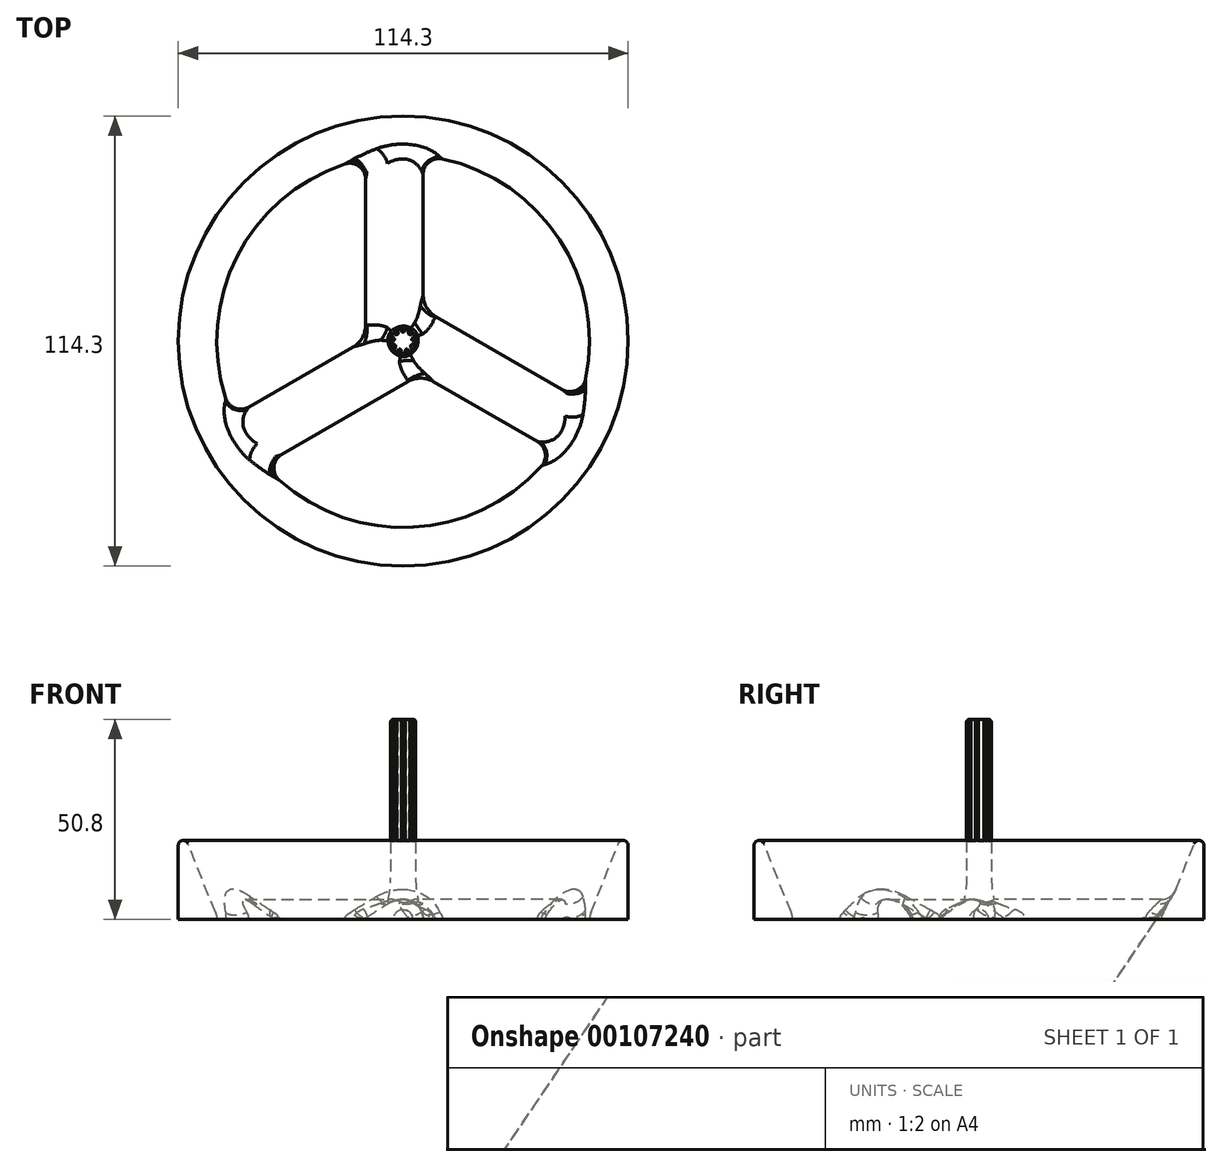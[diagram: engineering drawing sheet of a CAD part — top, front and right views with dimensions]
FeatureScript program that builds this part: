
annotation { "Feature Type Name" : "Feature", "Feature Type Description" : "" }
export const myFeature = defineFeature(function(context is Context, id is Id, definition is map)
    precondition{}
    {
        {
            var Q0;
            Q0=qCreatedBy(makeId("Front.planeOp"),FACE);
            var sketch = newSketch(context, id + "F0", { "sketchPlane" : qUnion([Q0])});
            skLineSegment(sketch, "E0", {"start": v(0, 0) * mm, "end": v(0, 50.8) * mm});
            skPoint(sketch, "E1.visualSharp", {"position": v(57.15, 25.4) * mm});
            skPoint(sketch, "E2.visualSharp", {"position": v(3.17, 50.8) * mm});
            skPoint(sketch, "E3.visualSharp", {"position": v(57.15, 0) * mm});
            skLineSegment(sketch, "E4.trimOffspring", {"start": v(3.17, -2.8) * mm, "end": v(3.17, -2.92) * mm});
            skArc(sketch, "E5", {"start": v(5.08, 0) * mm, "mid": v(3.6, 3.6) * mm, "end": v(0, 5.08) * mm});
            skLineSegment(sketch, "E6", {"start": v(57.15, 18.8) * mm, "end": v(57.15, 0) * mm});
            skLineSegment(sketch, "E7", {"start": v(57.15, 0) * mm, "end": v(47.35, 0) * mm});
            skLineSegment(sketch, "E8", {"start": v(47.7, 1.75) * mm, "end": v(54.7, 19.28) * mm});
            skArc(sketch, "E9", {"start": v(47.7, 1.75) * mm, "mid": v(47.44, 0.9) * mm, "end": v(47.35, 0) * mm});
            skPoint(sketch, "E10.orphan", {"position": v(47, 0) * mm});
            skArc(sketch, "E11.filletArc", {"start": v(57.15, 18.8) * mm, "mid": v(56.12, 20.05) * mm, "end": v(54.7, 19.28) * mm});
            skEllipticalArc(sketch, "E12", {});
            skLineSegment(sketch, "E13", {"start": v(-6.35, 0) * mm, "end": v(-2.48, 0) * mm});
            skPoint(sketch, "E14.orphan", {"position": v(6.35, 0) * mm});
            skLineSegment(sketch, "E15", {"start": v(3.18, 50.16) * mm, "end": v(3.18, 3.97) * mm});
            skLineSegment(sketch, "E16", {"start": v(2.54, 50.8) * mm, "end": v(0, 50.8) * mm});
            skArc(sketch, "E17.filletArc", {"start": v(3.17, 50.16) * mm, "mid": v(2.99, 50.61) * mm, "end": v(2.54, 50.8) * mm});
            skArc(sketch, "E18", {"start": v(2.48, 0) * mm, "mid": v(0, 2.48) * mm, "end": v(-2.48, 0) * mm});
            skLineSegment(sketch, "E19.trimOffspring", {"start": v(2.48, 0) * mm, "end": v(5.08, 0) * mm});
            skLineSegment(sketch, "E20", {"start": v(-2.48, 0) * mm, "end": v(2.48, 0) * mm});
            skArc(sketch, "E21", {"start": v(-9.24, 0.53) * mm, "mid": v(-9.45, 0.3) * mm, "end": v(-9.53, 0) * mm});
            skLineSegment(sketch, "E22", {"start": v(-9.24, 0.53) * mm, "end": v(-4.01, 3.94) * mm});
            skLineSegment(sketch, "E23", {"start": v(-6.35, 0) * mm, "end": v(-9.53, 0) * mm});
            skArc(sketch, "E24", {"start": v(3.17, 10.6) * mm, "mid": v(3.58, 6.12) * mm, "end": v(4.76, 1.77) * mm});
            const initialGuessF0  = {"E12": [0, 0, 0, 1, 0.00508, 0.00635, 6.283185307179586, 0.6836937466880189]};
            skSetInitialGuess(sketch, initialGuessF0);
            skSolve(sketch);
        }
        {
            var Q0;
            Q0=makeQuery(id+"F0.imprint","IMPRINT",FACE,{"disambiguationData":[TD([[makeQuery(id+"F0.imprint","IMPRINT",EDGE,{"derivedFrom":sQuery(id+"F0.wireOp",EDGE,"E6")}),-1.0]])]});
            var Q1;
            {var subQ0=sQuery(id+"F0.wireOp",EDGE,"E16");Q1=makeQuery(id+"F0.imprint","IMPRINT",FACE,{"disambiguationData":[TD([[makeQuery(id+"F0.imprint","IMPRINT",EDGE,{"derivedFrom":subQ0}),1.0]])]});}
            var Q2;
            {var subQ0=sQuery(id+"F0.wireOp",EDGE,"E13");var subQ3=sQuery(id+"F0.wireOp",EDGE,"E5");var subQ5=makeQuery(id+"F0.imprint","INTERSECT",VERTEX,{"derivedFrom":[subQ3,subQ0]});Q2=makeQuery(id+"F0.imprint","IMPRINT",FACE,{"disambiguationData":[TD([[makeQuery(id+"F0.imprint","IMPRINT",EDGE,{"disambiguationData":[TD([[subQ5,-1.0]])],"derivedFrom":subQ3}),1.0]])]});}
            var Q3;
            {var subQ3=sQuery(id+"F0.wireOp",EDGE,"E24");Q3=makeQuery(id+"F0.imprint","IMPRINT",FACE,{"disambiguationData":[TD([[makeQuery(id+"F0.imprint","IMPRINT",EDGE,{"derivedFrom":subQ3}),-1.0]])]});}
            var Q4;
            Q4=sQuery(id+"F0.wireOp",EDGE,"E0");
            revolve(context, id + "F1", {"entities" : qUnion([Q0, Q1, Q2, Q3]), "axis" : qUnion([Q4]), "revolveType" : RevolveType.FULL});
        }
        {
            var Q0;
            Q0=qCreatedBy(makeId("Top.planeOp"),FACE);
            var sketch = newSketch(context, id + "F2", { "sketchPlane" : qUnion([Q0])});
            skCircle(sketch, "E25.cCircle", {"center": v(0, 3.18) * mm, "radius": 0.64 * mm, "construction": true});
            skLineSegment(sketch, "E25.0", {"start": v(-1.1, 3.81) * mm, "end": v(1.1, 3.81) * mm});
            skLineSegment(sketch, "E25.1", {"start": v(0.69, 3.1) * mm, "end": v(0.27, 2.38) * mm});
            skLineSegment(sketch, "E25.2", {"start": v(-0.27, 2.38) * mm, "end": v(-0.69, 3.1) * mm});
            skPoint(sketch, "E25.0.midPoint", {"position": v(0, 3.81) * mm});
            skPoint(sketch, "E26.visualSharp", {"position": v(0, 1.9) * mm});
            skArc(sketch, "E26.filletArc", {"start": v(-0.27, 2.38) * mm, "mid": v(0, 2.22) * mm, "end": v(0.27, 2.38) * mm});
            skLineSegment(sketch, "E27.1.1", {"start": v(-1.46, 2.82) * mm, "end": v(-1.32, 2) * mm});
            skArc(sketch, "E27.1.2", {"start": v(-1.74, 1.65) * mm, "mid": v(-1.43, 1.7) * mm, "end": v(-1.32, 2) * mm});
            skLineSegment(sketch, "E27.1.3", {"start": v(-1.74, 1.65) * mm, "end": v(-2.52, 1.93) * mm});
            skLineSegment(sketch, "E27.2.1", {"start": v(-2.93, 1.22) * mm, "end": v(-2.3, 0.68) * mm});
            skArc(sketch, "E27.2.2", {"start": v(-2.4, 0.14) * mm, "mid": v(-2.19, 0.39) * mm, "end": v(-2.3, 0.68) * mm});
            skLineSegment(sketch, "E27.2.3", {"start": v(-2.4, 0.14) * mm, "end": v(-3.17, -0.14) * mm});
            skLineSegment(sketch, "E27.3.1", {"start": v(-3.03, -0.95) * mm, "end": v(-2.2, -0.95) * mm});
            skArc(sketch, "E27.3.2", {"start": v(-1.92, -1.43) * mm, "mid": v(-1.92, -1.11) * mm, "end": v(-2.2, -0.95) * mm});
            skLineSegment(sketch, "E27.3.3", {"start": v(-1.92, -1.43) * mm, "end": v(-2.34, -2.15) * mm});
            skLineSegment(sketch, "E27.4.1", {"start": v(-1.7, -2.68) * mm, "end": v(-1.07, -2.14) * mm});
            skArc(sketch, "E27.4.2", {"start": v(-0.56, -2.33) * mm, "mid": v(-0.76, -2.09) * mm, "end": v(-1.07, -2.14) * mm});
            skLineSegment(sketch, "E27.4.3", {"start": v(-0.56, -2.33) * mm, "end": v(-0.41, -3.15) * mm});
            skLineSegment(sketch, "E27.5.1", {"start": v(0.41, -3.15) * mm, "end": v(0.56, -2.33) * mm});
            skArc(sketch, "E27.5.2", {"start": v(1.07, -2.14) * mm, "mid": v(0.76, -2.09) * mm, "end": v(0.56, -2.33) * mm});
            skLineSegment(sketch, "E27.5.3", {"start": v(1.07, -2.14) * mm, "end": v(1.7, -2.68) * mm});
            skLineSegment(sketch, "E27.6.1", {"start": v(2.34, -2.15) * mm, "end": v(1.92, -1.43) * mm});
            skArc(sketch, "E27.6.2", {"start": v(2.2, -0.95) * mm, "mid": v(1.92, -1.11) * mm, "end": v(1.92, -1.43) * mm});
            skLineSegment(sketch, "E27.6.3", {"start": v(2.2, -0.95) * mm, "end": v(3.03, -0.95) * mm});
            skLineSegment(sketch, "E27.7.1", {"start": v(3.17, -0.14) * mm, "end": v(2.4, 0.14) * mm});
            skArc(sketch, "E27.7.2", {"start": v(2.3, 0.68) * mm, "mid": v(2.19, 0.39) * mm, "end": v(2.4, 0.14) * mm});
            skLineSegment(sketch, "E27.7.3", {"start": v(2.3, 0.68) * mm, "end": v(2.93, 1.22) * mm});
            skLineSegment(sketch, "E27.8.1", {"start": v(2.52, 1.93) * mm, "end": v(1.74, 1.65) * mm});
            skArc(sketch, "E27.8.2", {"start": v(1.32, 2) * mm, "mid": v(1.43, 1.7) * mm, "end": v(1.74, 1.65) * mm});
            skLineSegment(sketch, "E27.8.3", {"start": v(1.32, 2) * mm, "end": v(1.46, 2.82) * mm});
            skPoint(sketch, "E27.center", {"position": v(0, 0) * mm});
            skArc(sketch, "E28.trimOffspring", {"start": v(2.93, 1.22) * mm, "mid": v(2.75, 1.59) * mm, "end": v(2.52, 1.93) * mm});
            skArc(sketch, "E29", {"start": v(-2.93, 1.22) * mm, "mid": v(-3.13, 0.55) * mm, "end": v(-3.17, -0.14) * mm});
            skArc(sketch, "E30.trimOffspring", {"start": v(-3.03, -0.95) * mm, "mid": v(-2.75, -1.59) * mm, "end": v(-2.34, -2.15) * mm});
            skArc(sketch, "E31.trimOffspring", {"start": v(-1.7, -2.68) * mm, "mid": v(-1.09, -2.98) * mm, "end": v(-0.41, -3.15) * mm});
            skArc(sketch, "E32.trimOffspring", {"start": v(0.41, -3.15) * mm, "mid": v(1.09, -2.98) * mm, "end": v(1.7, -2.68) * mm});
            skArc(sketch, "E33.trimOffspring", {"start": v(2.34, -2.15) * mm, "mid": v(2.75, -1.59) * mm, "end": v(3.03, -0.95) * mm});
            skArc(sketch, "E34.trimOffspring", {"start": v(3.17, -0.14) * mm, "mid": v(3.13, 0.55) * mm, "end": v(2.93, 1.22) * mm});
            skArc(sketch, "E35.trimOffspring", {"start": v(2.52, 1.93) * mm, "mid": v(2.04, 2.43) * mm, "end": v(1.46, 2.82) * mm});
            skArc(sketch, "E36.trimOffspring", {"start": v(0.69, 3.1) * mm, "mid": v(0, 3.18) * mm, "end": v(-0.69, 3.1) * mm});
            skArc(sketch, "E37.trimOffspring", {"start": v(-1.46, 2.82) * mm, "mid": v(-2.04, 2.43) * mm, "end": v(-2.52, 1.93) * mm});
            skSolve(sketch);
        }
        {
            var Q0;
            Q0=makeQuery(id+"F2.imprint","IMPRINT",FACE,{"disambiguationData":[TD([[makeQuery(id+"F2.imprint","IMPRINT",EDGE,{"derivedFrom":sQuery(id+"F2.wireOp",EDGE,"E27.1.1")}),-1.0]])]});
            var Q1;
            Q1=makeQuery(id+"F2.imprint","IMPRINT",FACE,{"disambiguationData":[TD([[makeQuery(id+"F2.imprint","IMPRINT",EDGE,{"derivedFrom":sQuery(id+"F2.wireOp",EDGE,"E27.2.1")}),-1.0]])]});
            var Q2;
            Q2=makeQuery(id+"F2.imprint","IMPRINT",FACE,{"disambiguationData":[TD([[makeQuery(id+"F2.imprint","IMPRINT",EDGE,{"derivedFrom":sQuery(id+"F2.wireOp",EDGE,"E27.3.1")}),-1.0]])]});
            var Q3;
            Q3=makeQuery(id+"F2.imprint","IMPRINT",FACE,{"disambiguationData":[TD([[makeQuery(id+"F2.imprint","IMPRINT",EDGE,{"derivedFrom":sQuery(id+"F2.wireOp",EDGE,"E27.4.1")}),-1.0]])]});
            var Q4;
            Q4=makeQuery(id+"F2.imprint","IMPRINT",FACE,{"disambiguationData":[TD([[makeQuery(id+"F2.imprint","IMPRINT",EDGE,{"derivedFrom":sQuery(id+"F2.wireOp",EDGE,"E27.5.1")}),-1.0]])]});
            var Q5;
            Q5=makeQuery(id+"F2.imprint","IMPRINT",FACE,{"disambiguationData":[TD([[makeQuery(id+"F2.imprint","IMPRINT",EDGE,{"derivedFrom":sQuery(id+"F2.wireOp",EDGE,"E27.6.1")}),-1.0]])]});
            var Q6;
            Q6=makeQuery(id+"F2.imprint","IMPRINT",FACE,{"disambiguationData":[TD([[makeQuery(id+"F2.imprint","IMPRINT",EDGE,{"derivedFrom":sQuery(id+"F2.wireOp",EDGE,"E27.7.1")}),-1.0]])]});
            var Q7;
            Q7=makeQuery(id+"F2.imprint","IMPRINT",FACE,{"disambiguationData":[TD([[makeQuery(id+"F2.imprint","IMPRINT",EDGE,{"derivedFrom":sQuery(id+"F2.wireOp",EDGE,"E27.8.1")}),-1.0]])]});
            var Q8;
            Q8=makeQuery(id+"F2.imprint","IMPRINT",FACE,{"disambiguationData":[TD([[makeQuery(id+"F2.imprint","IMPRINT",EDGE,{"derivedFrom":sQuery(id+"F2.wireOp",EDGE,"E25.1")}),-1.0]])]});
            extrude(context, id + "F3", {"entities" : qUnion([Q0, Q1, Q2, Q3, Q4, Q5, Q6, Q7, Q8]), "depth" : 52.98 * mm, "hasSecondDirection" : true, "secondDirectionOppositeDirection" : false, "secondDirectionDepth" : 19.8 * mm});
        }
        {
            var Q0;
            Q0=makeQuery(id+"F3.opExtrude","SWEPT_BODY",BODY,{"disambiguationData":[OSD([sQuery(id+"F2.wireOp",EDGE,"E25.1"),sQuery(id+"F2.wireOp",EDGE,"E25.2"),sQuery(id+"F2.wireOp",EDGE,"E26.filletArc"),sQuery(id+"F2.wireOp",EDGE,"E36.trimOffspring")])]});
            var Q1;
            Q1=makeQuery(id+"F3.opExtrude","SWEPT_BODY",BODY,{"disambiguationData":[OSD([sQuery(id+"F2.wireOp",EDGE,"E27.1.1"),sQuery(id+"F2.wireOp",EDGE,"E27.1.2"),sQuery(id+"F2.wireOp",EDGE,"E27.1.3"),sQuery(id+"F2.wireOp",EDGE,"E37.trimOffspring")])]});
            var Q2;
            Q2=makeQuery(id+"F3.opExtrude","SWEPT_BODY",BODY,{"disambiguationData":[OSD([sQuery(id+"F2.wireOp",EDGE,"E27.2.1"),sQuery(id+"F2.wireOp",EDGE,"E27.2.2"),sQuery(id+"F2.wireOp",EDGE,"E27.2.3"),sQuery(id+"F2.wireOp",EDGE,"E29")])]});
            var Q3;
            Q3=makeQuery(id+"F3.opExtrude","SWEPT_BODY",BODY,{"disambiguationData":[OSD([sQuery(id+"F2.wireOp",EDGE,"E27.3.1"),sQuery(id+"F2.wireOp",EDGE,"E27.3.2"),sQuery(id+"F2.wireOp",EDGE,"E27.3.3"),sQuery(id+"F2.wireOp",EDGE,"E30.trimOffspring")])]});
            var Q4;
            Q4=makeQuery(id+"F3.opExtrude","SWEPT_BODY",BODY,{"disambiguationData":[OSD([sQuery(id+"F2.wireOp",EDGE,"E27.4.1"),sQuery(id+"F2.wireOp",EDGE,"E27.4.2"),sQuery(id+"F2.wireOp",EDGE,"E27.4.3"),sQuery(id+"F2.wireOp",EDGE,"E31.trimOffspring")])]});
            var Q5;
            Q5=makeQuery(id+"F3.opExtrude","SWEPT_BODY",BODY,{"disambiguationData":[OSD([sQuery(id+"F2.wireOp",EDGE,"E27.5.1"),sQuery(id+"F2.wireOp",EDGE,"E27.5.2"),sQuery(id+"F2.wireOp",EDGE,"E27.5.3"),sQuery(id+"F2.wireOp",EDGE,"E32.trimOffspring")])]});
            var Q6;
            Q6=makeQuery(id+"F3.opExtrude","SWEPT_BODY",BODY,{"disambiguationData":[OSD([sQuery(id+"F2.wireOp",EDGE,"E27.6.1"),sQuery(id+"F2.wireOp",EDGE,"E27.6.2"),sQuery(id+"F2.wireOp",EDGE,"E27.6.3"),sQuery(id+"F2.wireOp",EDGE,"E33.trimOffspring")])]});
            var Q7;
            Q7=makeQuery(id+"F3.opExtrude","SWEPT_BODY",BODY,{"disambiguationData":[OSD([sQuery(id+"F2.wireOp",EDGE,"E27.7.1"),sQuery(id+"F2.wireOp",EDGE,"E27.7.2"),sQuery(id+"F2.wireOp",EDGE,"E27.7.3"),sQuery(id+"F2.wireOp",EDGE,"E34.trimOffspring")])]});
            var Q8;
            Q8=makeQuery(id+"F3.opExtrude","SWEPT_BODY",BODY,{"disambiguationData":[OSD([sQuery(id+"F2.wireOp",EDGE,"E27.8.1"),sQuery(id+"F2.wireOp",EDGE,"E27.8.2"),sQuery(id+"F2.wireOp",EDGE,"E27.8.3"),sQuery(id+"F2.wireOp",EDGE,"E35.trimOffspring")])]});
            var Q9;
            Q9=makeQuery(id+"F1.opRevolve","SWEPT_BODY",BODY,{"disambiguationData":[OSD([sQuery(id+"F0.wireOp",EDGE,"E0"),sQuery(id+"F0.wireOp",EDGE,"b3ONHT4w-OPow-9vU2-dpi0-BedZ4xwEnRj7"),sQuery(id+"F0.wireOp",EDGE,"p2YjdxvI-C5U7-OCFZ-hL64-xagieLWP2dRE"),sQuery(id+"F0.wireOp",EDGE,"VkDzLiis-1y0P-EC4v-6lOs-WA2rIGYTaX5n"),sQuery(id+"F0.wireOp",EDGE,"E1.filletArc"),sQuery(id+"F0.wireOp",EDGE,"JwA5gNNF-Fkhf-Ru8d-CYqG-uIPYKwcStdHp"),sQuery(id+"F0.wireOp",EDGE,"VJsSlwMf-gpDe-zVnm-X9U3-KcMJw3opwtFv"),sQuery(id+"F0.wireOp",EDGE,"HwvpKeuE-Alte-Yzym-qIkG-h49GgYpIJdb7"),sQuery(id+"F0.wireOp",EDGE,"DyEhc6b5-tTjb-xtmK-yai0-PdHcH9X1jMEJ"),sQuery(id+"F0.wireOp",EDGE,"bZUXDXMF-OsGU-dvAX-A2zm-Hi4g4pJf9ipG"),sQuery(id+"F0.wireOp",EDGE,"Bh9XdUdV-DYBC-IwOP-javF-A2Mwh1VeRbNr"),sQuery(id+"F0.wireOp",EDGE,"BRNRaonm-3wnL-6FvH-YjtP-XJqQMA16pj4Z"),sQuery(id+"F0.wireOp",EDGE,"Ep8JvLHv-uFUy-Ba5m-8iN5-KwKFA3qrer0D"),sQuery(id+"F0.wireOp",EDGE,"277ba7a1-e97e-4eb0-947e-70daba67afde.filletArc"),sQuery(id+"F0.wireOp",EDGE,"f8218160-7506-4df3-a77c-66ee1f658aee.filletArc"),sQuery(id+"F0.wireOp",EDGE,"E2.filletArc")])]});
            booleanBodies(context, id + "F4", {"operationType" : BooleanOperationType.SUBTRACTION, "tools" : qUnion([Q0, Q1, Q2, Q3, Q4, Q5, Q6, Q7, Q8]), "targets" : qUnion([Q9])});
        }
        {
            var Q0;
            {var subQ0=sQuery(id+"F0.wireOp",EDGE,"E13");var subQ3=sQuery(id+"F0.wireOp",EDGE,"E5");var subQ5=makeQuery(id+"F0.imprint","INTERSECT",VERTEX,{"derivedFrom":[subQ3,subQ0]});Q0=makeQuery(id+"F0.imprint","IMPRINT",FACE,{"disambiguationData":[TD([[makeQuery(id+"F0.imprint","IMPRINT",EDGE,{"disambiguationData":[TD([[subQ5,-1.0]])],"derivedFrom":subQ3}),1.0]])]});}
            var Q1;
            {var subQ3=sQuery(id+"F0.wireOp",EDGE,"E12");Q1=makeQuery(id+"F0.imprint","IMPRINT",FACE,{"disambiguationData":[TD([[makeQuery(id+"F0.imprint","IMPRINT",EDGE,{"derivedFrom":subQ3}),1.0]])]});}
            var Q2;
            {var subQ0=sQuery(id+"F0.wireOp",EDGE,"E20");var subQ1=sQuery(id+"F0.wireOp",EDGE,"E0");var subQ2=makeQuery(id+"F0.imprint","INTERSECT",VERTEX,{"derivedFrom":[subQ1,subQ0]});Q2=makeQuery(id+"F0.imprint","IMPRINT",FACE,{"disambiguationData":[TD([[makeQuery(id+"F0.imprint","IMPRINT",EDGE,{"disambiguationData":[TD([[subQ2,-1.0]])],"derivedFrom":subQ1}),1.0]])]});}
            var Q3;
            {var subQ0=sQuery(id+"F0.wireOp",EDGE,"E20");var subQ1=sQuery(id+"F0.wireOp",EDGE,"E0");var subQ2=makeQuery(id+"F0.imprint","INTERSECT",VERTEX,{"derivedFrom":[subQ1,subQ0]});Q3=makeQuery(id+"F0.imprint","IMPRINT",FACE,{"disambiguationData":[TD([[makeQuery(id+"F0.imprint","IMPRINT",EDGE,{"disambiguationData":[TD([[subQ2,-1.0]])],"derivedFrom":subQ1}),-1.0]])]});}
            extrude(context, id + "F5", {"entities" : qUnion([Q0, Q1, Q2, Q3]), "oppositeDirection" : true, "depth" : 53.62 * mm, "hasSecondDirection" : true, "secondDirectionOppositeDirection" : false, "secondDirectionDepth" : 2.54 * mm});
        }
        {
            var Q0;
            Q0=makeQuery(id+"F5.opExtrude","SWEPT_BODY",BODY,{"disambiguationData":[OSD([sQuery(id+"F0.wireOp",EDGE,"E5"),sQuery(id+"F0.wireOp",EDGE,"E12"),sQuery(id+"F0.wireOp",EDGE,"E13")])]});
            var Q1;
            Q1=sQuery(id+"F0.wireOp",EDGE,"E0");
            circularPattern(context, id + "F6", {"entities" : qUnion([Q0]), "axis" : qUnion([Q1]), "angle" : 360 * degree, "instanceCount" : 3, "equalSpace" : true});
        }
        {
            var Q0;
            Q0=makeQuery(id+"F6.opPattern","COPY",BODY,{"derivedFrom":makeQuery(id+"F5.opExtrude","SWEPT_BODY",BODY,{"disambiguationData":[OSD([sQuery(id+"F0.wireOp",EDGE,"E5"),sQuery(id+"F0.wireOp",EDGE,"E12"),sQuery(id+"F0.wireOp",EDGE,"E13")])]}),"instanceName":"2"});
            var Q1;
            Q1=makeQuery(id+"F5.opExtrude","SWEPT_BODY",BODY,{"disambiguationData":[OSD([sQuery(id+"F0.wireOp",EDGE,"E5"),sQuery(id+"F0.wireOp",EDGE,"E12"),sQuery(id+"F0.wireOp",EDGE,"E13")])]});
            var Q2;
            Q2=makeQuery(id+"F6.opPattern","COPY",BODY,{"derivedFrom":makeQuery(id+"F5.opExtrude","SWEPT_BODY",BODY,{"disambiguationData":[OSD([sQuery(id+"F0.wireOp",EDGE,"E5"),sQuery(id+"F0.wireOp",EDGE,"E12"),sQuery(id+"F0.wireOp",EDGE,"E13")])]}),"instanceName":"1"});
            var Q3;
            Q3=makeQuery(id+"F1.opRevolve","SWEPT_BODY",BODY,{"disambiguationData":[OSD([sQuery(id+"F0.wireOp",EDGE,"E6"),sQuery(id+"F0.wireOp",EDGE,"E7"),sQuery(id+"F0.wireOp",EDGE,"E8"),sQuery(id+"F0.wireOp",EDGE,"E9"),sQuery(id+"F0.wireOp",EDGE,"E11.filletArc")])]});
            var Q4;
            Q4=makeQuery(id+"F1.opRevolve","SWEPT_BODY",BODY,{"disambiguationData":[OSD([sQuery(id+"F0.wireOp",EDGE,"E0"),sQuery(id+"F0.wireOp",EDGE,"E5"),sQuery(id+"F0.wireOp",EDGE,"E13"),sQuery(id+"F0.wireOp",EDGE,"E15"),sQuery(id+"F0.wireOp",EDGE,"E16"),sQuery(id+"F0.wireOp",EDGE,"E17.filletArc")])]});
            booleanBodies(context, id + "F7", {"operationType" : BooleanOperationType.UNION, "tools" : qUnion([Q0, Q1, Q2, Q3, Q4])});
        }
        {
            var Q0;
            Q0=makeQuery(id+"F7.opBoolean","INTERSECT",EDGE,{"derivedFrom":[makeQuery(id+"F5.opExtrude","SWEPT_FACE",FACE,{"disambiguationData":[OSD([sQuery(id+"F0.wireOp",EDGE,"E12")])]}),makeQuery(id+"F6.opPattern","COPY",FACE,{"derivedFrom":makeQuery(id+"F5.opExtrude","SWEPT_FACE",FACE,{"disambiguationData":[OSD([sQuery(id+"F0.wireOp",EDGE,"E5")])]}),"instanceName":"1"})]});
            var Q1;
            Q1=makeQuery(id+"F7.opBoolean","INTERSECT",EDGE,{"derivedFrom":[makeQuery(id+"F5.opExtrude","SWEPT_FACE",FACE,{"disambiguationData":[OSD([sQuery(id+"F0.wireOp",EDGE,"E5")])]}),makeQuery(id+"F6.opPattern","COPY",FACE,{"derivedFrom":makeQuery(id+"F5.opExtrude","SWEPT_FACE",FACE,{"disambiguationData":[OSD([sQuery(id+"F0.wireOp",EDGE,"E12")])]}),"instanceName":"2"})]});
            var Q2;
            Q2=makeQuery(id+"F7.opBoolean","INTERSECT",EDGE,{"derivedFrom":[makeQuery(id+"F6.opPattern","COPY",FACE,{"derivedFrom":makeQuery(id+"F5.opExtrude","SWEPT_FACE",FACE,{"disambiguationData":[OSD([sQuery(id+"F0.wireOp",EDGE,"E12")])]}),"instanceName":"1"}),makeQuery(id+"F6.opPattern","COPY",FACE,{"derivedFrom":makeQuery(id+"F5.opExtrude","SWEPT_FACE",FACE,{"disambiguationData":[OSD([sQuery(id+"F0.wireOp",EDGE,"E5")])]}),"instanceName":"2"})]});
            fillet(context, id + "F8", {"entities" : qUnion([Q0, Q1, Q2]), "radius" : 6.35 * mm, "tangentPropagation" : true, "allowEdgeOverflow" : false});
        }
        {
            var Q0;
            Q0=makeQuery(id+"F7.opBoolean","INTERSECT",EDGE,{"derivedFrom":[makeQuery(id+"F1.opRevolve","SWEPT_FACE",FACE,{"disambiguationData":[OSD([sQuery(id+"F0.wireOp",EDGE,"E15")])]}),makeQuery(id+"F6.opPattern","COPY",FACE,{"derivedFrom":makeQuery(id+"F5.opExtrude","SWEPT_FACE",FACE,{"disambiguationData":[OSD([sQuery(id+"F0.wireOp",EDGE,"E12")])]}),"instanceName":"2"})]});
            var Q1;
            Q1=makeQuery(id+"F7.opBoolean","INTERSECT",EDGE,{"derivedFrom":[makeQuery(id+"F1.opRevolve","SWEPT_FACE",FACE,{"disambiguationData":[OSD([sQuery(id+"F0.wireOp",EDGE,"E8")])]}),makeQuery(id+"F6.opPattern","COPY",FACE,{"derivedFrom":makeQuery(id+"F5.opExtrude","SWEPT_FACE",FACE,{"disambiguationData":[OSD([sQuery(id+"F0.wireOp",EDGE,"E5")])]}),"instanceName":"2"})]});
            var Q2;
            Q2=makeQuery(id+"F7.opBoolean","INTERSECT",EDGE,{"derivedFrom":[makeQuery(id+"F1.opRevolve","SWEPT_FACE",FACE,{"disambiguationData":[OSD([sQuery(id+"F0.wireOp",EDGE,"E8")])]}),makeQuery(id+"F5.opExtrude","SWEPT_FACE",FACE,{"disambiguationData":[OSD([sQuery(id+"F0.wireOp",EDGE,"E12")])]})]});
            var Q3;
            Q3=makeQuery(id+"F7.opBoolean","INTERSECT",EDGE,{"derivedFrom":[makeQuery(id+"F1.opRevolve","SWEPT_FACE",FACE,{"disambiguationData":[OSD([sQuery(id+"F0.wireOp",EDGE,"E8")])]}),makeQuery(id+"F6.opPattern","COPY",FACE,{"derivedFrom":makeQuery(id+"F5.opExtrude","SWEPT_FACE",FACE,{"disambiguationData":[OSD([sQuery(id+"F0.wireOp",EDGE,"E12")])]}),"instanceName":"1"})]});
            fillet(context, id + "F9", {"entities" : qUnion([Q0, Q1, Q2, Q3]), "radius" : 4.06 * mm, "tangentPropagation" : true, "allowEdgeOverflow" : false});
        }
        {
            var Q0;
            {var subQ0=sQuery(id+"F0.wireOp",EDGE,"E20");var subQ1=sQuery(id+"F0.wireOp",EDGE,"E0");var subQ2=makeQuery(id+"F0.imprint","INTERSECT",VERTEX,{"derivedFrom":[subQ1,subQ0]});Q0=makeQuery(id+"F0.imprint","IMPRINT",FACE,{"disambiguationData":[TD([[makeQuery(id+"F0.imprint","IMPRINT",EDGE,{"disambiguationData":[TD([[subQ2,-1.0]])],"derivedFrom":subQ1}),1.0]])]});}
            var Q1;
            Q1=sQuery(id+"F0.wireOp",EDGE,"E0");
            revolve(context, id + "F10", {"entities" : qUnion([Q0]), "axis" : qUnion([Q1]), "revolveType" : RevolveType.FULL});
        }
        {
            var Q0;
            Q0=makeQuery(id+"F10.opRevolve","SWEPT_BODY",BODY,{"disambiguationData":[OSD([sQuery(id+"F0.wireOp",EDGE,"E0"),sQuery(id+"F0.wireOp",EDGE,"E18"),sQuery(id+"F0.wireOp",EDGE,"E20")])]});
            var Q1;
            Q1=makeQuery(id+"F6.opPattern","COPY",BODY,{"derivedFrom":makeQuery(id+"F5.opExtrude","SWEPT_BODY",BODY,{"disambiguationData":[OSD([sQuery(id+"F0.wireOp",EDGE,"E5"),sQuery(id+"F0.wireOp",EDGE,"E12"),sQuery(id+"F0.wireOp",EDGE,"E13"),sQuery(id+"F0.wireOp",EDGE,"E19.trimOffspring"),sQuery(id+"F0.wireOp",EDGE,"E20")])]}),"instanceName":"2"});
            booleanBodies(context, id + "F11", {"operationType" : BooleanOperationType.SUBTRACTION, "tools" : qUnion([Q0]), "targets" : qUnion([Q1])});
        }
    });
